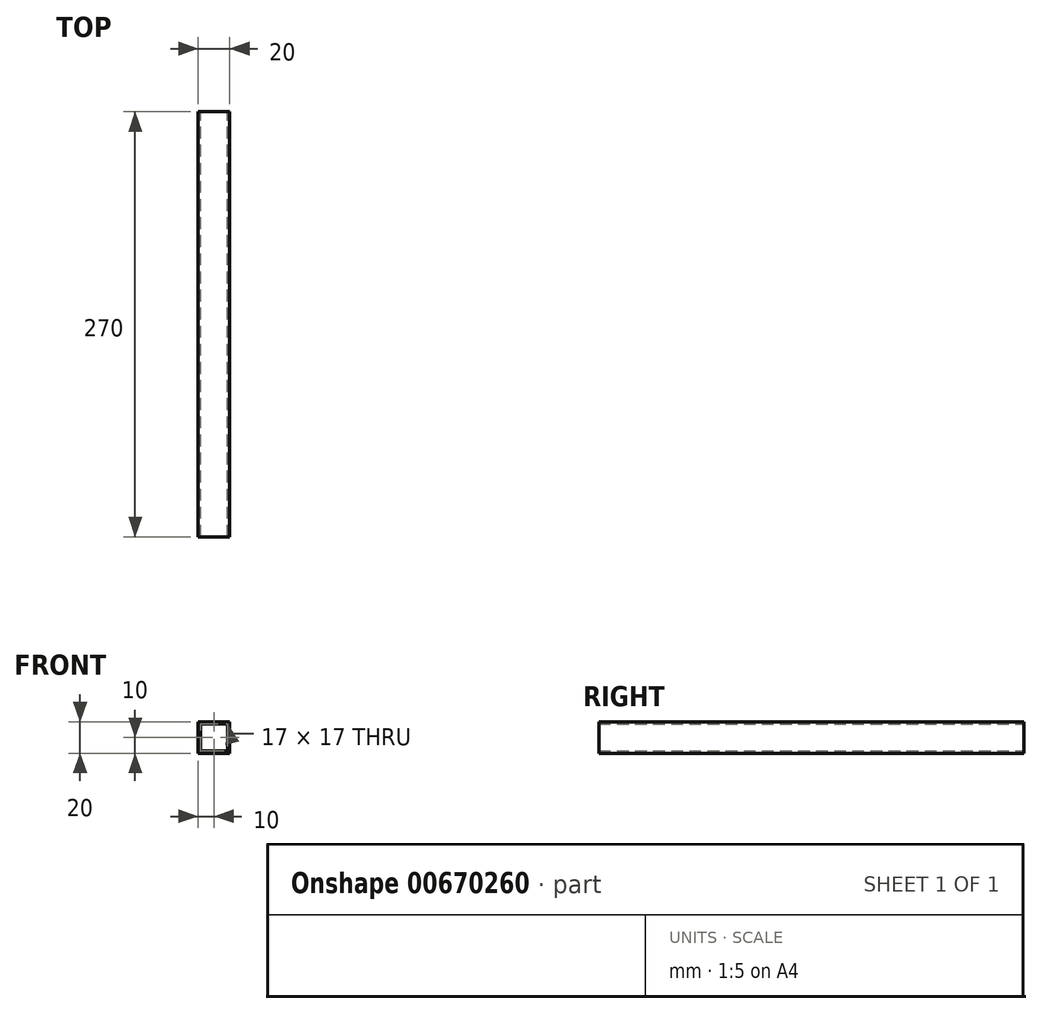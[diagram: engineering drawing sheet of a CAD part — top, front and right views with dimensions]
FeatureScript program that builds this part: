
annotation { "Feature Type Name" : "Feature", "Feature Type Description" : "" }
export const myFeature = defineFeature(function(context is Context, id is Id, definition is map)
    precondition{}
    {
        {
            var Q0;
            Q0=qCreatedBy(makeId("Front.planeOp"),FACE);
            var sketch = newSketch(context, id + "F0", { "sketchPlane" : qUnion([Q0])});
            skLineSegment(sketch, "E0.bottom", {"start": v(-10, 10) * mm, "end": v(10, 10) * mm});
            skLineSegment(sketch, "E0.top", {"start": v(-10, -10) * mm, "end": v(10, -10) * mm});
            skLineSegment(sketch, "E0.left", {"start": v(-10, 10) * mm, "end": v(-10, -10) * mm});
            skLineSegment(sketch, "E0.right", {"start": v(10, 10) * mm, "end": v(10, -10) * mm});
            skLineSegment(sketch, "E1.bottom", {"start": v(-8.5, 8.5) * mm, "end": v(8.5, 8.5) * mm});
            skLineSegment(sketch, "E1.top", {"start": v(-8.5, -8.5) * mm, "end": v(8.5, -8.5) * mm});
            skLineSegment(sketch, "E1.left", {"start": v(-8.5, 8.5) * mm, "end": v(-8.5, -8.5) * mm});
            skLineSegment(sketch, "E1.right", {"start": v(8.5, 8.5) * mm, "end": v(8.5, -8.5) * mm});
            skSolve(sketch);
        }
        {
            var Q0;
            Q0=qSketchRegion(id+"F0",true);
            extrude(context, id + "F1", {"entities" : qUnion([Q0]), "depth" : 270 * mm, "offsetDistance" : 25 * mm});
        }
    });
